# Revit family: Hand_Shower_System-American_Standard-Spectra-9238759_Series
name_source: partatom
category: Plumbing Fixtures
revit_build: Autodesk Revit 2018 (Build: 20170223_1515(x64)
units: mm (PartAtom-declared; Revit-internal decimal feet)

## family parameters
Cut with Voids When Loaded = No
Host = Face
OmniClass Number = 23.45.05.14.17
OmniClass Title = Showers
Part Type = Normal
Room Calculation Point = No
Round Connector Dimension = Use Diameter
Shared = Yes

## types (2) — shared parameters
Assembly Code = D2010710
CW Connection = No
CWFU = 3
Default Elevation = 74"
Description = Spectra 24-In. 4-Spray 1.8 GPM Hand Shower Rail System with Filter
Flow Rate = 1.8 gpm (6.8 L/min)
HW Connection = No
HWFU = 3
Height = 24"
IAPMO Compliance = ASME A112.18.1, CSA B125.1
Inlet Connection Diameter = 1/2"
Inlet Connection Radius = 1/4"
Installation Type = Wall Mounted
Length = 5 7/16"
Manufacturer = American Standard
Pressure Range = 20 – 125 psi (0.7 – 8.6 bar)
Price = Prices may vary. Please consult Manufacturer Representative for most up-to-date price list.
Product Documentation Link = https://americanstandard.box.com
Product Page URL = https://www.americanstandard-us.com
Temperature = 50 - 150°F (10 - 66°C)
Tempered Water Connection = Yes
URL = https://www.americanstandard-us.com
Vent Connection = No
WFU = 4
Waste Connection = No
Width = 5 1/4"
cUPC Compliant = Yes

## per-type parameters (varying)
| type | Finish | Material |
| 9238759.002 | Metal-American Standard-002-Polished Chrome | Metal-American Standard-002-Polished Chrome |
| 9238759.295 | Metal-American Standard-295-Brushed Nickel | Metal-American Standard-295-Brushed Nickel |

note: column(s) folded — value = type name in every type: Model

## geometry (parser evidence)
native form markers: Sweep x4
no freeform markers — native parametric forms only
